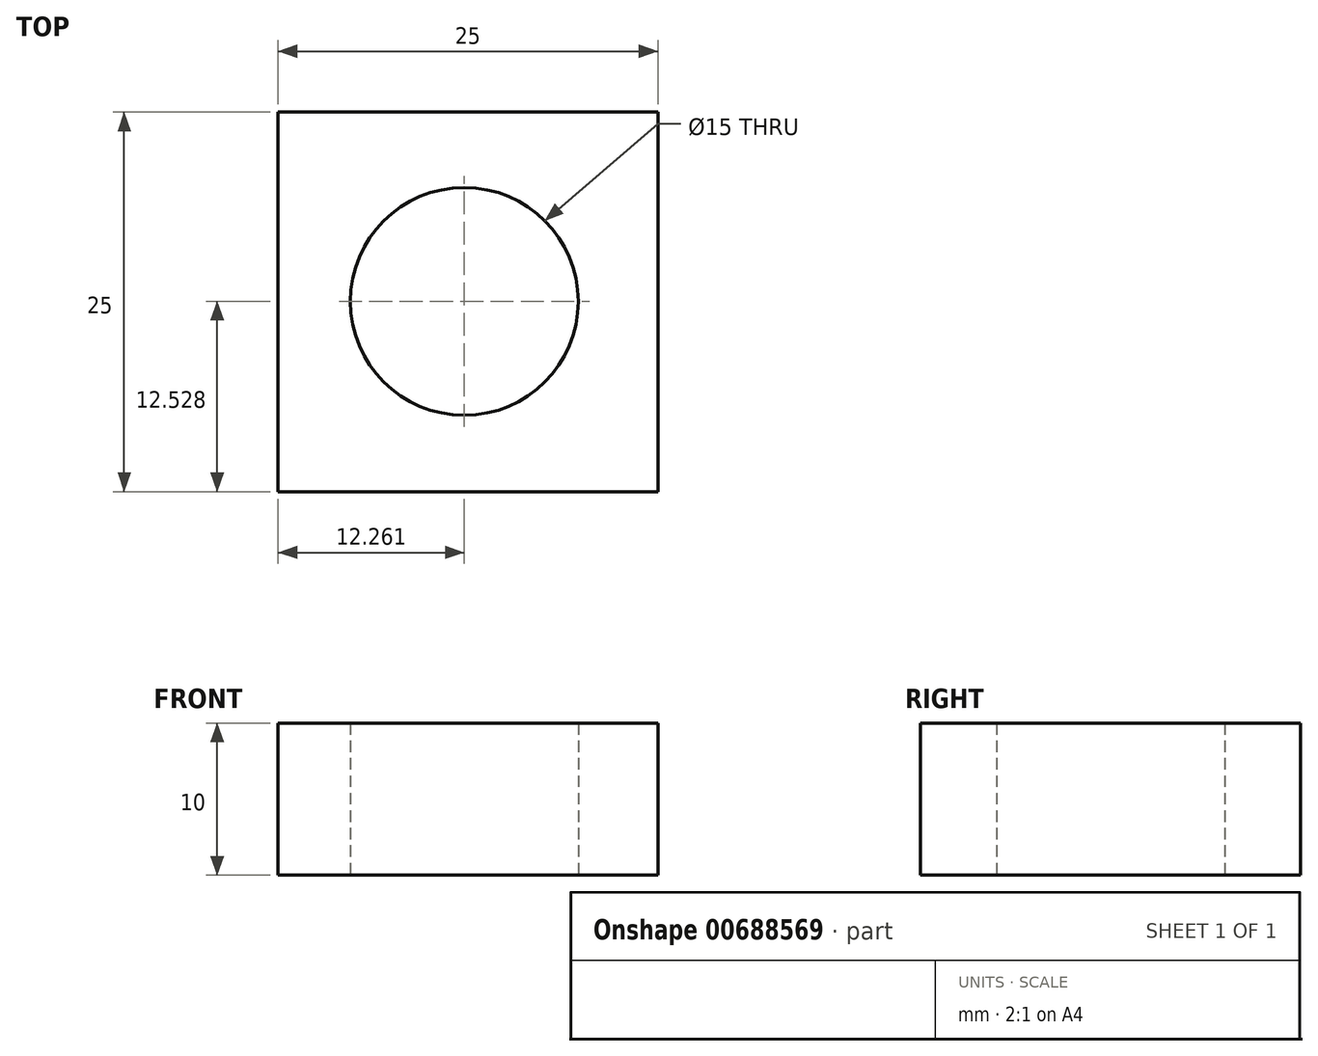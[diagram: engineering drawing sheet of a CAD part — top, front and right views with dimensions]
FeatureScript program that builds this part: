
annotation { "Feature Type Name" : "Feature", "Feature Type Description" : "" }
export const myFeature = defineFeature(function(context is Context, id is Id, definition is map)
    precondition{}
    {
        {
            var Q0;
            Q0=qCreatedBy(makeId("Top.planeOp"),FACE);
            var sketch = newSketch(context, id + "F0", { "sketchPlane" : qUnion([Q0])});
            skLineSegment(sketch, "E0.bottom", {"start": v(-17.02, 12.36) * mm, "end": v(7.98, 12.36) * mm});
            skLineSegment(sketch, "E0.top", {"start": v(-17.02, -12.64) * mm, "end": v(7.98, -12.64) * mm});
            skLineSegment(sketch, "E0.left", {"start": v(-17.02, 12.36) * mm, "end": v(-17.02, -12.64) * mm});
            skLineSegment(sketch, "E0.right", {"start": v(7.98, 12.36) * mm, "end": v(7.98, -12.64) * mm});
            skSolve(sketch);
        }
        {
            var Q0;
            Q0=makeQuery(id+"F0.imprint","IMPRINT",FACE,{"disambiguationData":[TD([[makeQuery(id+"F0.imprint","IMPRINT",EDGE,{"derivedFrom":sQuery(id+"F0.wireOp",EDGE,"E0.bottom")}),-1.0]])]});
            var sketch = newSketch(context, id + "F1", { "sketchPlane" : qUnion([Q0])});
            skCircle(sketch, "E1", {"center": v(-4.76, -0.11) * mm, "radius": 7.5 * mm});
            skSolve(sketch);
        }
        {
            var Q0;
            Q0=makeQuery(id+"F1.imprint","IMPRINT",FACE,{"disambiguationData":[TD([[makeQuery(id+"F1.imprint","IMPRINT",EDGE,{"derivedFrom":sQuery(id+"F1.wireOp",EDGE,"E1")}),-1.0]])]});
            extrude(context, id + "F2", {"entities" : qUnion([Q0]), "depth" : 10 * mm});
        }
    });
